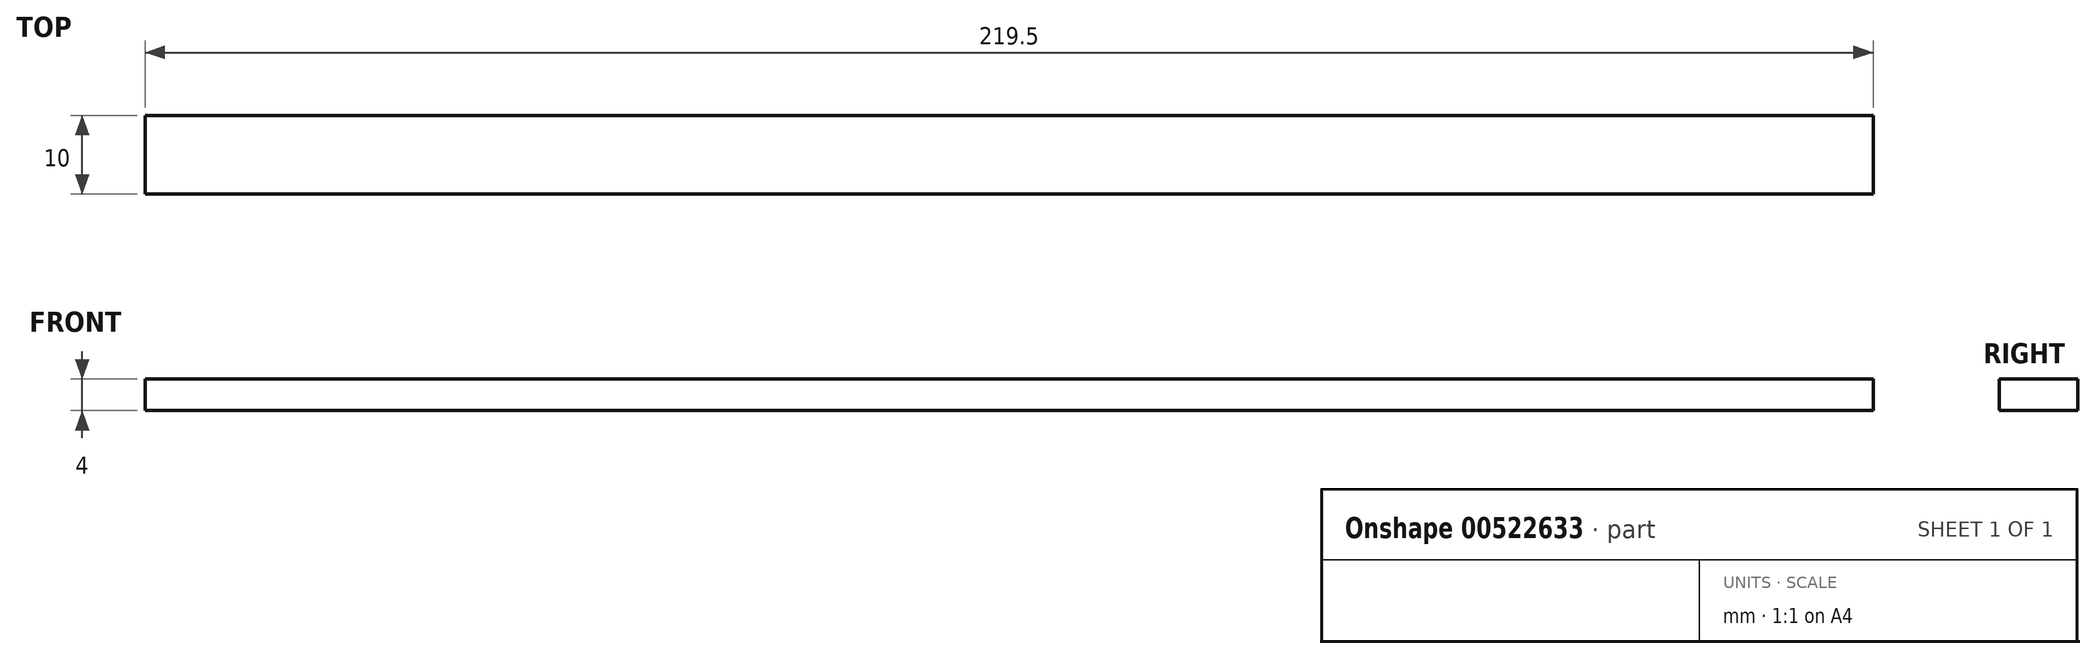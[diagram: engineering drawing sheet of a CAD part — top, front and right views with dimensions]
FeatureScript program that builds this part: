
annotation { "Feature Type Name" : "Feature", "Feature Type Description" : "" }
export const myFeature = defineFeature(function(context is Context, id is Id, definition is map)
    precondition{}
    {
        {
            var Q0;
            Q0=qCreatedBy(makeId("Top.planeOp"),FACE);
            var sketch = newSketch(context, id + "F0", { "sketchPlane" : qUnion([Q0])});
            skLineSegment(sketch, "E0.bottom", {"start": v(-106.44, 5.83) * mm, "end": v(113.06, 5.83) * mm});
            skLineSegment(sketch, "E0.top", {"start": v(-106.44, -4.17) * mm, "end": v(113.06, -4.17) * mm});
            skLineSegment(sketch, "E0.left", {"start": v(-106.44, 5.83) * mm, "end": v(-106.44, -4.17) * mm});
            skLineSegment(sketch, "E0.right", {"start": v(113.06, 5.83) * mm, "end": v(113.06, -4.17) * mm});
            skSolve(sketch);
        }
        {
            var Q0;
            Q0=makeQuery(id+"F0.imprint","IMPRINT",FACE,{"disambiguationData":[TD([[makeQuery(id+"F0.imprint","IMPRINT",EDGE,{"derivedFrom":sQuery(id+"F0.wireOp",EDGE,"E0.bottom")}),-1.0]])]});
            extrude(context, id + "F1", {"entities" : qUnion([Q0]), "endBound" : BoundingType.SYMMETRIC, "depth" : 4 * mm, "offsetDistance" : 25 * mm});
        }
    });
